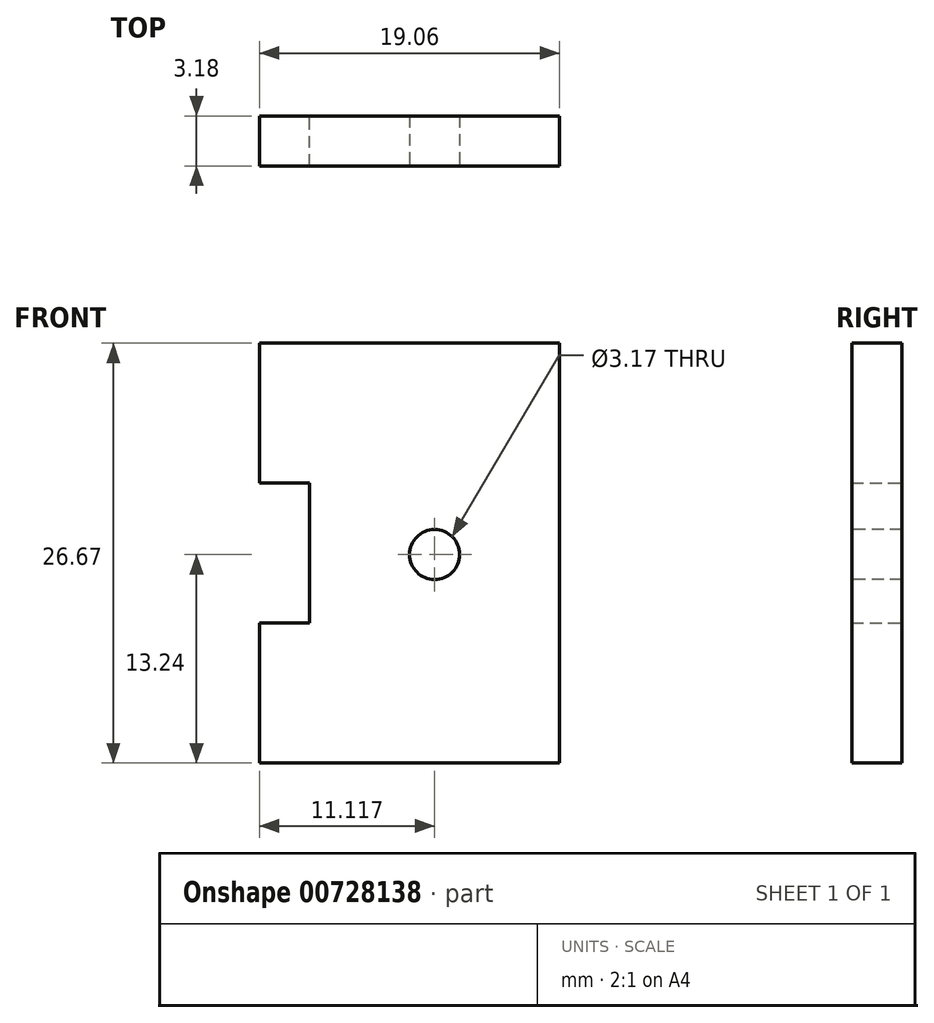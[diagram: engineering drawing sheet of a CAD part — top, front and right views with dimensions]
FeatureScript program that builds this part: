
annotation { "Feature Type Name" : "Feature", "Feature Type Description" : "" }
export const myFeature = defineFeature(function(context is Context, id is Id, definition is map)
    precondition{}
    {
        {
            var Q0;
            Q0=qCreatedBy(makeId("Front.planeOp"),FACE);
            var sketch = newSketch(context, id + "F0", { "sketchPlane" : qUnion([Q0])});
            skLineSegment(sketch, "E0.bottom", {"start": v(9.52, 38.1) * mm, "end": v(-9.53, 38.1) * mm});
            skLineSegment(sketch, "E0.top", {"start": v(9.53, -38.1) * mm, "end": v(-9.52, -38.1) * mm});
            skLineSegment(sketch, "E0.left", {"start": v(9.52, 38.1) * mm, "end": v(9.53, -38.1) * mm});
            skLineSegment(sketch, "E0.right", {"start": v(-9.53, 38.1) * mm, "end": v(-9.52, -38.1) * mm});
            skPoint(sketch, "E0.middle", {"position": v(0, 0) * mm});
            skLineSegment(sketch, "E1", {"start": v(-6.35, 38.1) * mm, "end": v(-6.35, -38.1) * mm});
            skLineSegment(sketch, "E2", {"start": v(-9.53, 29.2) * mm, "end": v(-6.35, 29.2) * mm});
            skLineSegment(sketch, "E3", {"start": v(-9.53, 20.32) * mm, "end": v(-6.35, 20.32) * mm});
            skLineSegment(sketch, "E4", {"start": v(-9.53, 11.43) * mm, "end": v(-6.35, 11.43) * mm});
            skLineSegment(sketch, "E5", {"start": v(-9.53, -1.27) * mm, "end": v(-6.35, -1.27) * mm});
            skLineSegment(sketch, "E6", {"start": v(-9.52, -13.97) * mm, "end": v(-6.35, -13.97) * mm});
            skLineSegment(sketch, "E7", {"start": v(-6.35, 11.43) * mm, "end": v(9.53, 11.43) * mm});
            skSolve(sketch);
        }
        {
            var Q0;
            {var subQ5=sQuery(id+"F0.wireOp",EDGE,"QXyYzKvK-Vf3k-rWq0-lT2y-zqTFrBfQWzn5");Q0=makeQuery(id+"F0.imprint","IMPRINT",FACE,{"disambiguationData":[TD([[makeQuery(id+"F0.imprint","IMPRINT",EDGE,{"derivedFrom":subQ5}),1.0]])]});}
            var Q1;
            {var subQ5=sQuery(id+"F0.wireOp",EDGE,"E7");Q1=makeQuery(id+"F0.imprint","IMPRINT",FACE,{"disambiguationData":[TD([[makeQuery(id+"F0.imprint","IMPRINT",EDGE,{"derivedFrom":subQ5}),1.0]])]});}
            var Q2;
            {var subQ5=sQuery(id+"F0.wireOp",EDGE,"E2");Q2=makeQuery(id+"F0.imprint","IMPRINT",FACE,{"disambiguationData":[TD([[makeQuery(id+"F0.imprint","IMPRINT",EDGE,{"derivedFrom":subQ5}),1.0]])]});}
            var Q3;
            {var subQ0=sQuery(id+"F0.wireOp",EDGE,"E3");Q3=makeQuery(id+"F0.imprint","IMPRINT",FACE,{"disambiguationData":[TD([[makeQuery(id+"F0.imprint","IMPRINT",EDGE,{"derivedFrom":subQ0}),-1.0]])]});}
            extrude(context, id + "F1", {"entities" : qUnion([Q0, Q1, Q2, Q3]), "depth" : 3.17 * mm, "offsetDistance" : 25.4 * mm});
        }
        {
            var Q0;
            Q0=makeQuery(id+"F1.opExtrude","CAP_FACE",FACE,{"disambiguationData":[OSD([sQuery(id+"F0.wireOp",EDGE,"E0.bottom"),sQuery(id+"F0.wireOp",EDGE,"E0.top"),sQuery(id+"F0.wireOp",EDGE,"E0.left"),sQuery(id+"F0.wireOp",EDGE,"E0.right"),sQuery(id+"F0.wireOp",EDGE,"E1"),sQuery(id+"F0.wireOp",EDGE,"E2"),sQuery(id+"F0.wireOp",EDGE,"E3"),sQuery(id+"F0.wireOp",EDGE,"E4"),sQuery(id+"F0.wireOp",EDGE,"E5"),sQuery(id+"F0.wireOp",EDGE,"E6")])],"isStart":false});
            var sketch = newSketch(context, id + "F2", { "sketchPlane" : qUnion([Q0])});
            skCircle(sketch, "E8", {"center": v(1.59, 24.67) * mm, "radius": 1.59 * mm});
            skSolve(sketch);
        }
        {
            var Q0;
            Q0 = qSketchRegion(id + "F2", true);
            extrude(context, id + "F3", {"entities" : qUnion([Q0]), "operationType" : NewBodyOperationType.REMOVE, "endBound" : BoundingType.THROUGH_ALL, "oppositeDirection" : true, "depth" : 25.4 * mm, "offsetDistance" : 25.4 * mm});
        }
    });
